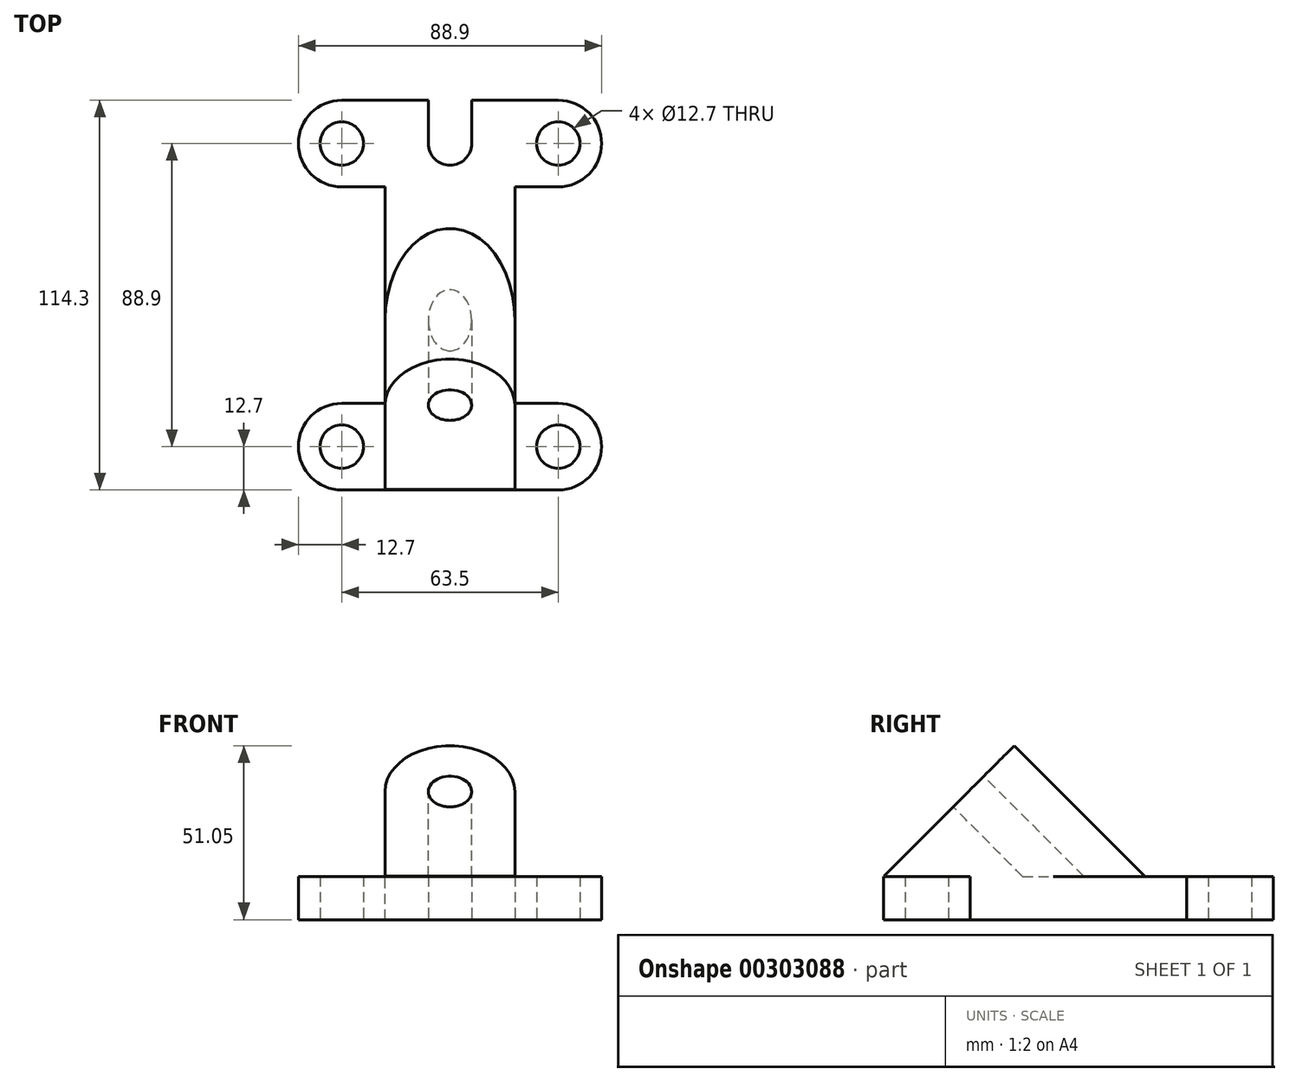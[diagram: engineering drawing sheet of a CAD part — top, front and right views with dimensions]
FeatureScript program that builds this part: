
annotation { "Feature Type Name" : "Feature", "Feature Type Description" : "" }
export const myFeature = defineFeature(function(context is Context, id is Id, definition is map)
    precondition{}
    {
        {
            var Q0;
            Q0=qCreatedBy(makeId("Top.planeOp"),FACE);
            var sketch = newSketch(context, id + "F0", { "sketchPlane" : qUnion([Q0])});
            skCircle(sketch, "E0", {"center": v(0, 0) * mm, "radius": 6.35 * mm});
            skCircle(sketch, "E1", {"center": v(0, 0) * mm, "radius": 12.7 * mm});
            skLineSegment(sketch, "E2", {"start": v(0, 0) * mm, "end": v(63.5, 0) * mm});
            skCircle(sketch, "E3", {"center": v(63.5, 0) * mm, "radius": 6.35 * mm});
            skCircle(sketch, "E4", {"center": v(63.5, 0) * mm, "radius": 12.7 * mm});
            skLineSegment(sketch, "E5", {"start": v(0, -12.7) * mm, "end": v(63.5, -12.7) * mm});
            skCircle(sketch, "E6", {"center": v(0, 88.9) * mm, "radius": 12.7 * mm});
            skCircle(sketch, "E7", {"center": v(63.5, 88.9) * mm, "radius": 12.7 * mm});
            skCircle(sketch, "E8", {"center": v(0, 88.9) * mm, "radius": 6.35 * mm});
            skCircle(sketch, "E9", {"center": v(63.5, 88.9) * mm, "radius": 6.35 * mm});
            skLineSegment(sketch, "E10", {"start": v(0, 101.6) * mm, "end": v(63.5, 101.6) * mm});
            skLineSegment(sketch, "E11", {"start": v(31.75, 101.6) * mm, "end": v(31.75, 88.9) * mm});
            skCircle(sketch, "E12", {"center": v(31.75, 88.9) * mm, "radius": 6.35 * mm});
            skLineSegment(sketch, "E13", {"start": v(25.4, 88.9) * mm, "end": v(25.4, 101.6) * mm});
            skLineSegment(sketch, "E14", {"start": v(38.1, 88.9) * mm, "end": v(38.1, 101.6) * mm});
            skLineSegment(sketch, "E15", {"start": v(12.7, 88.9) * mm, "end": v(12.7, 0) * mm});
            skLineSegment(sketch, "E16", {"start": v(50.8, 88.9) * mm, "end": v(50.8, 0) * mm});
            skLineSegment(sketch, "E17", {"start": v(63.5, 12.7) * mm, "end": v(50.8, 12.7) * mm});
            skLineSegment(sketch, "E18", {"start": v(0, 12.7) * mm, "end": v(12.7, 12.7) * mm});
            skLineSegment(sketch, "E19", {"start": v(0, 76.2) * mm, "end": v(12.7, 76.2) * mm});
            skLineSegment(sketch, "E20", {"start": v(63.5, 76.2) * mm, "end": v(50.8, 76.2) * mm});
            skSolve(sketch);
        }
        {
            var Q0;
            {var subQ3=sQuery(id+"F0.wireOp",EDGE,"E18");Q0=makeQuery(id+"F0.imprint","IMPRINT",FACE,{"disambiguationData":[TD([[makeQuery(id+"F0.imprint","IMPRINT",EDGE,{"derivedFrom":subQ3}),-1.0]])]});}
            var Q1;
            {var subQ3=sQuery(id+"F0.wireOp",EDGE,"E17");Q1=makeQuery(id+"F0.imprint","IMPRINT",FACE,{"disambiguationData":[TD([[makeQuery(id+"F0.imprint","IMPRINT",EDGE,{"derivedFrom":subQ3}),1.0]])]});}
            var Q2;
            {var subQ3=sQuery(id+"F0.wireOp",EDGE,"E19");Q2=makeQuery(id+"F0.imprint","IMPRINT",FACE,{"disambiguationData":[TD([[makeQuery(id+"F0.imprint","IMPRINT",EDGE,{"derivedFrom":subQ3}),1.0]])]});}
            var Q3;
            {var subQ3=sQuery(id+"F0.wireOp",EDGE,"E20");Q3=makeQuery(id+"F0.imprint","IMPRINT",FACE,{"disambiguationData":[TD([[makeQuery(id+"F0.imprint","IMPRINT",EDGE,{"derivedFrom":subQ3}),-1.0]])]});}
            var Q4;
            Q4=makeQuery(id+"F0.imprint","IMPRINT",FACE,{"disambiguationData":[TD([[makeQuery(id+"F0.imprint","IMPRINT",EDGE,{"derivedFrom":sQuery(id+"F0.wireOp",EDGE,"E0")}),-1.0]])]});
            var Q5;
            {var subQ0=sQuery(id+"F0.wireOp",EDGE,"E5");Q5=makeQuery(id+"F0.imprint","IMPRINT",FACE,{"disambiguationData":[TD([[makeQuery(id+"F0.imprint","IMPRINT",EDGE,{"derivedFrom":subQ0}),1.0]])]});}
            var Q6;
            Q6=makeQuery(id+"F0.imprint","IMPRINT",FACE,{"disambiguationData":[TD([[makeQuery(id+"F0.imprint","IMPRINT",EDGE,{"derivedFrom":sQuery(id+"F0.wireOp",EDGE,"E3")}),-1.0]])]});
            var Q7;
            Q7=makeQuery(id+"F0.imprint","IMPRINT",FACE,{"disambiguationData":[TD([[makeQuery(id+"F0.imprint","IMPRINT",EDGE,{"derivedFrom":sQuery(id+"F0.wireOp",EDGE,"E8")}),-1.0]])]});
            var Q8;
            Q8=makeQuery(id+"F0.imprint","IMPRINT",FACE,{"disambiguationData":[TD([[makeQuery(id+"F0.imprint","IMPRINT",EDGE,{"derivedFrom":sQuery(id+"F0.wireOp",EDGE,"E9")}),-1.0]])]});
            var Q9;
            {var subQ9=sQuery(id+"F0.wireOp",EDGE,"E13");Q9=makeQuery(id+"F0.imprint","IMPRINT",FACE,{"disambiguationData":[TD([[makeQuery(id+"F0.imprint","IMPRINT",EDGE,{"derivedFrom":subQ9}),1.0]])]});}
            extrude(context, id + "F1", {"entities" : qUnion([Q0, Q1, Q2, Q3, Q4, Q5, Q6, Q7, Q8, Q9]), "depth" : 12.7 * mm});
        }
        {
            var Q0;
            Q0=makeQuery(id+"F1.opExtrude","CAP_EDGE",EDGE,{"disambiguationData":[OSD([sQuery(id+"F0.wireOp",EDGE,"E5")])],"isStart":false});
            cPlane(context, id + "F2", {"entities" : qUnion([Q0]), "cplaneType" : CPlaneType.LINE_ANGLE, "offset" : 25.4 * mm, "angle" : 135 * degree, "width" : 152.4 * mm, "height" : 152.4 * mm});
        }
        {
            var Q0;
            Q0=qCreatedBy(id+"F2.planeOp",FACE);
            var sketch = newSketch(context, id + "F3", { "sketchPlane" : qUnion([Q0])});
            skLineSegment(sketch, "E21", {"start": v(12.7, 0.14) * mm, "end": v(12.7, 35.19) * mm});
            skLineSegment(sketch, "E22", {"start": v(12.7, 0.14) * mm, "end": v(50.8, 0.14) * mm});
            skLineSegment(sketch, "E23", {"start": v(0, 0) * mm, "end": v(12.7, 0.14) * mm});
            skLineSegment(sketch, "E24", {"start": v(12.7, 35.19) * mm, "end": v(50.8, 35.19) * mm});
            skLineSegment(sketch, "E25", {"start": v(50.8, 35.19) * mm, "end": v(50.8, 0.14) * mm});
            skCircle(sketch, "E26", {"center": v(31.75, 35.19) * mm, "radius": 19.05 * mm});
            skCircle(sketch, "E27", {"center": v(31.75, 35.19) * mm, "radius": 6.35 * mm});
            skSolve(sketch);
        }
        {
            var Q0;
            {var subQ1=sQuery(id+"F3.wireOp",EDGE,"E24");var subQ3=sQuery(id+"F3.wireOp",EDGE,"E27");var subQ4=makeQuery(id+"F3.imprint","INTERSECT",VERTEX,{"disambiguationData":[OD(0.0)],"derivedFrom":[subQ1,subQ3]});Q0=makeQuery(id+"F3.imprint","IMPRINT",FACE,{"disambiguationData":[TD([[makeQuery(id+"F3.imprint","IMPRINT",EDGE,{"disambiguationData":[TD([[subQ4,1.0]])],"derivedFrom":subQ3}),-1.0]])]});}
            var Q1;
            {var subQ0=sQuery(id+"F3.wireOp",EDGE,"E21");Q1=makeQuery(id+"F3.imprint","IMPRINT",FACE,{"disambiguationData":[TD([[makeQuery(id+"F3.imprint","IMPRINT",EDGE,{"derivedFrom":subQ0}),-1.0]])]});}
            var Q2;
            {var subQ1=sQuery(id+"F3.wireOp",EDGE,"E24");var subQ3=sQuery(id+"F3.wireOp",EDGE,"E27");var subQ4=makeQuery(id+"F3.imprint","INTERSECT",VERTEX,{"disambiguationData":[OD(0.0)],"derivedFrom":[subQ1,subQ3]});Q2=makeQuery(id+"F3.imprint","IMPRINT",FACE,{"disambiguationData":[TD([[makeQuery(id+"F3.imprint","IMPRINT",EDGE,{"disambiguationData":[TD([[subQ4,-1.0]])],"derivedFrom":subQ3}),-1.0]])]});}
            extrude(context, id + "F4", {"entities" : qUnion([Q0, Q1, Q2]), "operationType" : NewBodyOperationType.ADD, "oppositeDirection" : true, "depth" : 76.2 * mm});
        }
        {
            var Q0;
            Q0 = qSketchRegion(id + "F0", true);
            extrude(context, id + "F5", {"entities" : qUnion([Q0]), "operationType" : NewBodyOperationType.REMOVE, "oppositeDirection" : true, "depth" : 76.2 * mm});
        }
    });
